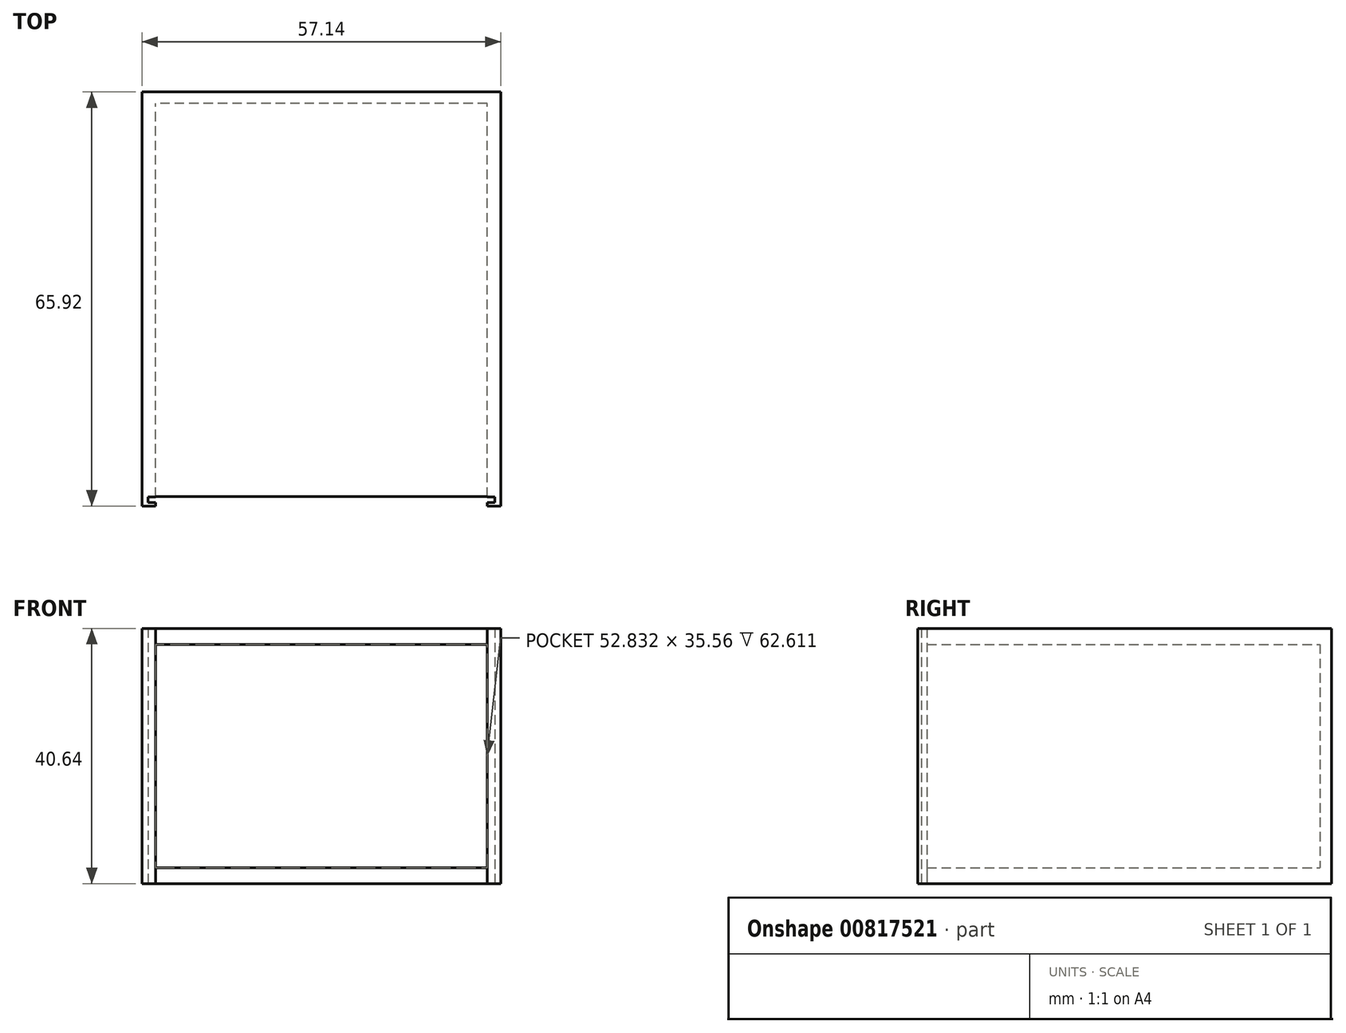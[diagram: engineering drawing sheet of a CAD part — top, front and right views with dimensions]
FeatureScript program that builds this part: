
annotation { "Feature Type Name" : "Feature", "Feature Type Description" : "" }
export const myFeature = defineFeature(function(context is Context, id is Id, definition is map)
    precondition{}
    {
        {
            var Q0;
            Q0=qCreatedBy(makeId("Top.planeOp"),FACE);
            var sketch = newSketch(context, id + "F0", { "sketchPlane" : qUnion([Q0])});
            skLineSegment(sketch, "E0.bottom", {"start": v(26.42, 31.12) * mm, "end": v(-26.42, 31.12) * mm});
            skLineSegment(sketch, "E0.top", {"start": v(26.42, -31.12) * mm, "end": v(-26.42, -31.12) * mm});
            skLineSegment(sketch, "E0.left", {"start": v(26.42, 31.12) * mm, "end": v(26.42, -31.12) * mm});
            skLineSegment(sketch, "E0.right", {"start": v(-26.42, 31.12) * mm, "end": v(-26.42, -31.12) * mm});
            skPoint(sketch, "E0.middle", {"position": v(0, 0) * mm});
            skLineSegment(sketch, "E1.bottom", {"start": v(28.57, 32.96) * mm, "end": v(-28.57, 32.96) * mm});
            skLineSegment(sketch, "E1.top", {"start": v(28.57, -32.96) * mm, "end": v(-28.57, -32.96) * mm});
            skLineSegment(sketch, "E1.left", {"start": v(28.57, 32.96) * mm, "end": v(28.57, -32.96) * mm});
            skLineSegment(sketch, "E1.right", {"start": v(-28.57, 32.96) * mm, "end": v(-28.57, -32.96) * mm});
            skLineSegment(sketch, "E2", {"start": v(26.42, -31.12) * mm, "end": v(26.42, -32.96) * mm});
            skLineSegment(sketch, "E3", {"start": v(-26.42, -31.12) * mm, "end": v(-26.42, -32.96) * mm});
            skLineSegment(sketch, "E4", {"start": v(0, 47.42) * mm, "end": v(0, -44.3) * mm});
            skLineSegment(sketch, "E5", {"start": v(26.42, -31.53) * mm, "end": v(27.61, -31.53) * mm});
            skLineSegment(sketch, "E6", {"start": v(26.42, -32.41) * mm, "end": v(27.61, -32.41) * mm});
            skLineSegment(sketch, "E7", {"start": v(27.61, -32.41) * mm, "end": v(27.61, -31.53) * mm});
            skLineSegment(sketch, "E8.MirrorCS", {"start": v(-26.42, -31.53) * mm, "end": v(-27.61, -31.53) * mm});
            skLineSegment(sketch, "E9.MirrorCS", {"start": v(-27.61, -32.41) * mm, "end": v(-27.61, -31.53) * mm});
            skLineSegment(sketch, "E10.MirrorCS", {"start": v(-26.42, -32.41) * mm, "end": v(-27.61, -32.41) * mm});
            skSolve(sketch);
        }
        {
            var Q0;
            {var subQ9=sQuery(id+"F0.wireOp",EDGE,"E0.left");Q0=makeQuery(id+"F0.imprint","IMPRINT",FACE,{"disambiguationData":[TD([[makeQuery(id+"F0.imprint","IMPRINT",EDGE,{"derivedFrom":subQ9}),1.0]])]});}
            var Q1;
            {var subQ10=sQuery(id+"F0.wireOp",EDGE,"E0.right");Q1=makeQuery(id+"F0.imprint","IMPRINT",FACE,{"disambiguationData":[TD([[makeQuery(id+"F0.imprint","IMPRINT",EDGE,{"derivedFrom":subQ10}),-1.0]])]});}
            extrude(context, id + "F1", {"entities" : qUnion([Q0, Q1]), "depth" : 40.64 * mm, "offsetDistance" : 25.4 * mm});
        }
        {
            var Q0;
            Q0=makeQuery(id+"F1.opExtrude","SWEPT_FACE",FACE,{"disambiguationData":[OSD([sQuery(id+"F0.wireOp",EDGE,"E0.bottom")])]});
            var sketch = newSketch(context, id + "F2", { "sketchPlane" : qUnion([Q0])});
            skLineSegment(sketch, "E11.bottom", {"start": v(26.42, 2.54) * mm, "end": v(-26.42, 2.54) * mm});
            skLineSegment(sketch, "E11.top", {"start": v(26.42, -2.54) * mm, "end": v(-26.42, -2.54) * mm});
            skLineSegment(sketch, "E11.left", {"start": v(26.42, 2.54) * mm, "end": v(26.42, -2.54) * mm});
            skLineSegment(sketch, "E11.right", {"start": v(-26.42, 2.54) * mm, "end": v(-26.42, -2.54) * mm});
            skPoint(sketch, "E11.middle", {"position": v(0, 0) * mm});
            skLineSegment(sketch, "E12.bottom", {"start": v(26.42, 38.1) * mm, "end": v(-26.42, 38.1) * mm});
            skLineSegment(sketch, "E12.top", {"start": v(26.42, 43.18) * mm, "end": v(-26.42, 43.18) * mm});
            skLineSegment(sketch, "E12.left", {"start": v(26.42, 38.1) * mm, "end": v(26.42, 43.18) * mm});
            skLineSegment(sketch, "E12.right", {"start": v(-26.42, 38.1) * mm, "end": v(-26.42, 43.18) * mm});
            skPoint(sketch, "E12.middle", {"position": v(0, 40.64) * mm});
            skSolve(sketch);
        }
        {
            var Q0;
            {var subQ0=sQuery(id+"F2.wireOp",EDGE,"E11.bottom");Q0=makeQuery(id+"F2.imprint","IMPRINT",FACE,{"disambiguationData":[TD([[makeQuery(id+"F2.imprint","IMPRINT",EDGE,{"derivedFrom":subQ0}),1.0]])]});}
            var Q1;
            {var subQ0=sQuery(id+"F2.wireOp",EDGE,"E12.bottom");Q1=makeQuery(id+"F2.imprint","IMPRINT",FACE,{"disambiguationData":[TD([[makeQuery(id+"F2.imprint","IMPRINT",EDGE,{"derivedFrom":subQ0}),-1.0]])]});}
            extrude(context, id + "F3", {"entities" : qUnion([Q0, Q1]), "operationType" : NewBodyOperationType.ADD, "depth" : 62.6 * mm, "offsetDistance" : 25.4 * mm});
        }
    });
